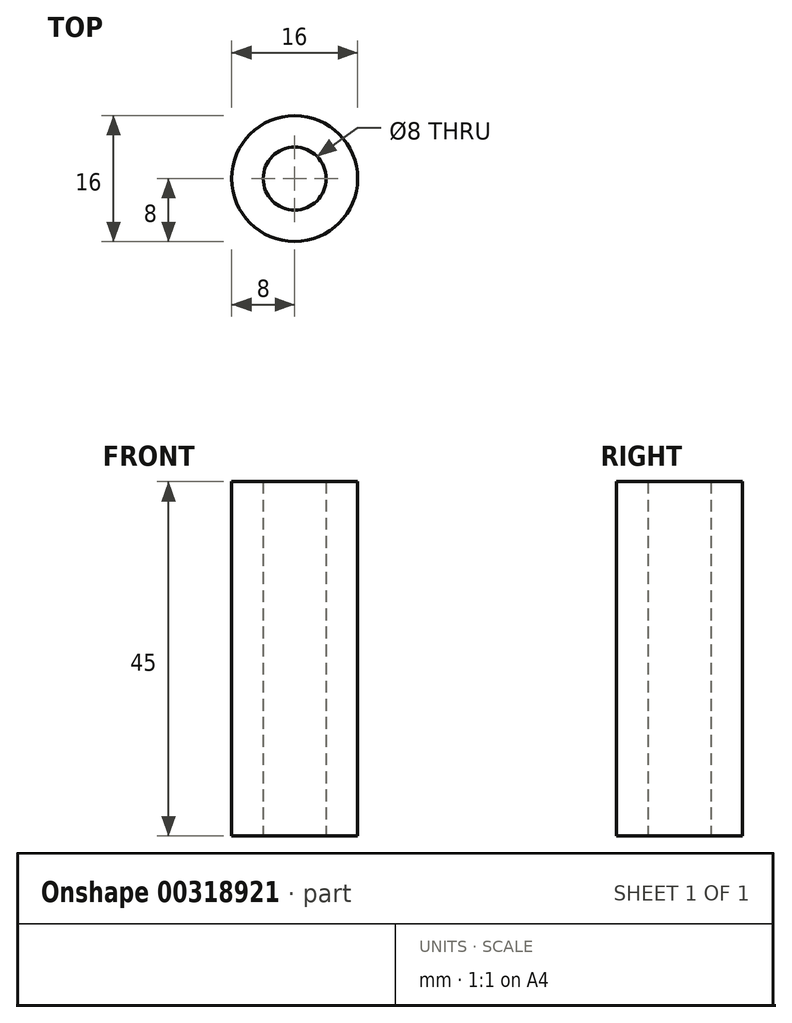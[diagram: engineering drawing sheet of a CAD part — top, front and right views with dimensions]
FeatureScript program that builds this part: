
annotation { "Feature Type Name" : "Feature", "Feature Type Description" : "" }
export const myFeature = defineFeature(function(context is Context, id is Id, definition is map)
    precondition{}
    {
        {
            var Q0;
            Q0=qCreatedBy(makeId("Top.planeOp"),FACE);
            var sketch = newSketch(context, id + "F0", { "sketchPlane" : qUnion([Q0])});
            skCircle(sketch, "E0", {"center": v(0, 0) * mm, "radius": 8 * mm});
            skCircle(sketch, "E1", {"center": v(0, 0) * mm, "radius": 4 * mm});
            skSolve(sketch);
        }
        {
            var Q0;
            Q0=makeQuery(id+"F0.imprint","IMPRINT",FACE,{"disambiguationData":[TD([[makeQuery(id+"F0.imprint","IMPRINT",EDGE,{"derivedFrom":sQuery(id+"F0.wireOp",EDGE,"E0")}),1.0]])]});
            extrude(context, id + "F1", {"entities" : qUnion([Q0]), "depth" : 45 * mm});
        }
    });
